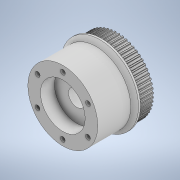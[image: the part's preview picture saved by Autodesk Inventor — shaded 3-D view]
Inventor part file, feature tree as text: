
AUTODESK INVENTOR PART (.ipt)
format: ipt  version: 2020.3 (Build 243373000, 373)  size: 858,624 bytes
history: native  units: mm
features: extrude x14, sketch x14, pattern_circular x4, mirror x1, chamfer x1
ambient origin geometry x8: Origin, YZ Plane, XZ Plane, XY Plane, X Axis, Y Axis, Z Axis, Center Point
bodies: Solid1 (feature_tree)
feature tree (34):
  extrude  "Extrusion1"  Depth=22.0mm
  extrude  "Extrusion2"  Depth=7.0mm
  extrude  "Extrusion3"  Depth=16.0mm
  extrude  "Extrusion4"  Depth=5.0mm
  extrude  "Extrusion5"  Depth=0.55mm
  mirror  "Mirror1"
  pattern_circular  "Circular Pattern1"  Count=60 Angle=360.0deg
  extrude  "Extrusion6"  Depth=14.0mm
  pattern_circular  "Circular Pattern2"  Count=3 Angle=360.0deg
  extrude  "Extrusion7"  Depth=7.2mm TaperAngle=0.0deg
  extrude  "Extrusion8"  Depth=7.0mm
  extrude  "Extrusion10"  Depth=7.0mm
  pattern_circular  "Circular Pattern4"  [2 undecoded]
  extrude  "Extrusion12"  Depth=7.0mm
  extrude  "Extrusion13"  Depth=7.0mm
  extrude  "Extrusion14"  Depth=7.0mm
  pattern_circular  "Circular Pattern5"  Count=8  [1 undecoded]
  extrude  "Extrusion15"  Depth=7.0mm
  chamfer  "Chamfer1"  [1 undecoded]
  extrude  "Extrusion16"  TaperAngle=120.0deg  [1 undecoded]
  sketch  "Sketch1"  dims[d0=40.0mm d1=22.0mm]
  sketch  "Sketch2"  dims[d2=7.0mm d3=0.0mm d4=8.6mm]
  sketch  "Sketch3"  dims[d5=16.0mm d6=0.0mm d7=180.0mm]
  sketch  "Sketch4"  dims[d8=5.0mm d9=0.0mm d10=22.0mm]
  sketch  "Sketch5"  dims[d11=7.0mm d12=0.0mm d14=0.55mm]
  sketch  "Sketch6"  dims[d17=0.4mm]
  sketch  "Sketch7"  dims[d18=0.75mm]
  sketch  "Sketch8"  dims[d19=0.15mm]
  sketch  "Sketch9"  dims[d20=0.523599mm]
  sketch  "Sketch11"  dims[d22=18.8mm]
  sketch  "Sketch12"  dims[d23=8.0mm d24=0.0mm d25=600.0mm d26=360.0deg]
  sketch  "Sketch13"  dims[d28=2.5mm d29=14.0mm]
  sketch  "Sketch14"  dims[d30=23.0mm d31=0.0mm d32=30.0mm d33=360.0deg]
  sketch  "Sketch16"  dims[d35=15.0mm d36=7.2mm d37=0.0mm d38=1.745329mm d39=0.872665mm d40=3.2mm d41=3.2mm d42=3.2mm d43=80.0mm d44=80.0mm d45=40.0mm d46=0.0mm d47=0.0mm d48=120.0deg d49=120.0deg d50=5.7mm d51=120.0deg d52=120.0deg d53=5.7mm d54=29.670597mm d55=120.0deg d60=5.7mm d61=120.0deg d62=120.0deg d63=0.872665mm d69=5.0mm d70=0.0mm d71=180.0mm d72=360.0deg d76=10.0mm d77=0.0mm d78=10.0mm d79=0.0mm d80=2.5mm d81=15.0mm d82=20.0mm d83=0.0mm d84=60.0mm d85=360.0deg d87=2.0mm d88=19.0mm d89=0.0mm d90=2.0mm d91=2.0mm d92=45.0deg d93=23.0mm d94=7.0mm d95=0.0mm d74=0.5mm d75=0.872665mm]
note: 5 required parameter values undecoded (feature->parameter linkage not recoverable at this tier; creation-order binding heuristic only, values carry confidence <= 0.55)
